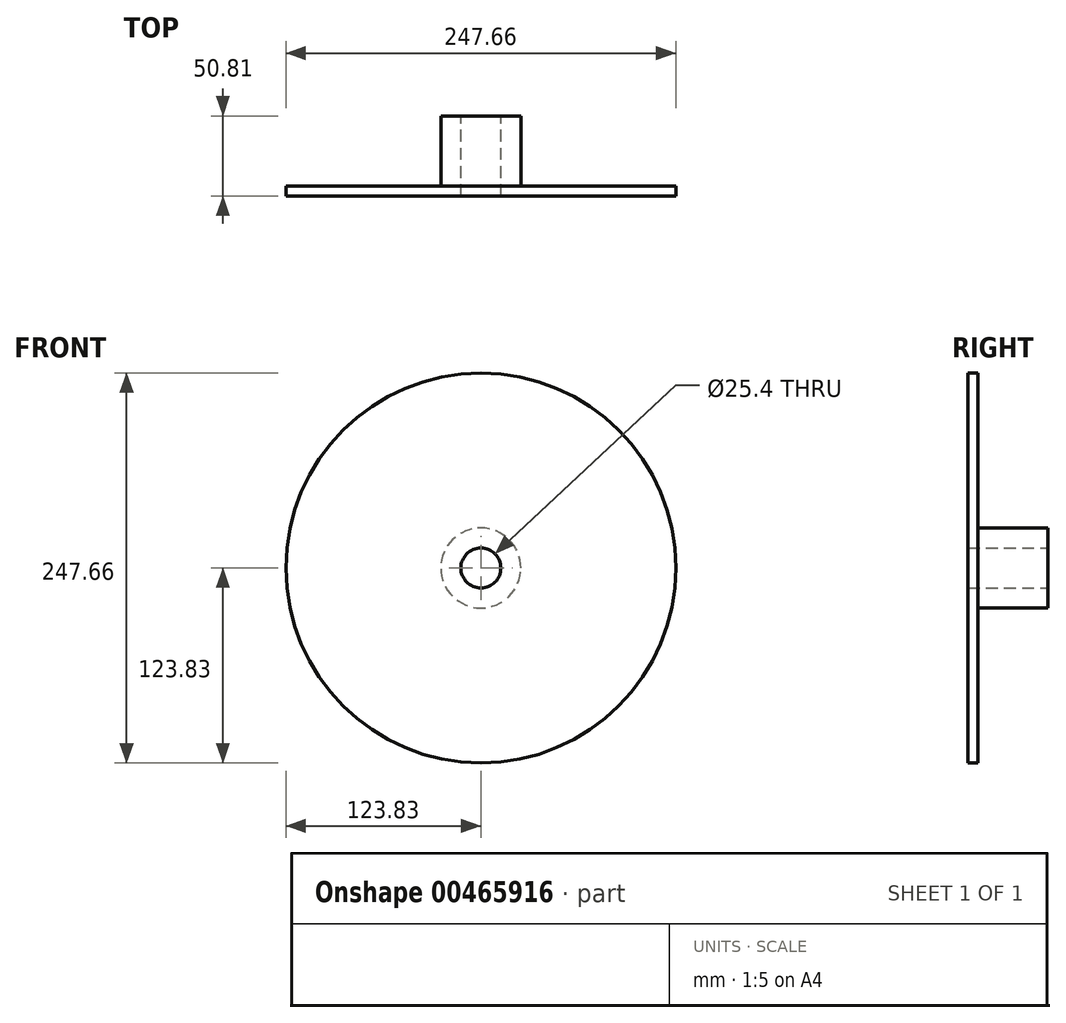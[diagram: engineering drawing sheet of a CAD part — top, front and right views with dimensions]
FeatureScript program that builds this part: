
annotation { "Feature Type Name" : "Feature", "Feature Type Description" : "" }
export const myFeature = defineFeature(function(context is Context, id is Id, definition is map)
    precondition{}
    {
        {
            var Q0;
            Q0=qCreatedBy(makeId("Front.planeOp"),FACE);
            var sketch = newSketch(context, id + "F0", { "sketchPlane" : qUnion([Q0])});
            skCircle(sketch, "E0", {"center": v(0, 0) * mm, "radius": 123.83 * mm});
            skSolve(sketch);
        }
        {
            var Q0;
            Q0=makeQuery(id+"F0.imprint","IMPRINT",FACE,{"disambiguationData":[TD([[makeQuery(id+"F0.imprint","IMPRINT",EDGE,{"derivedFrom":sQuery(id+"F0.wireOp",EDGE,"E0")}),1.0]])]});
            extrude(context, id + "F1", {"entities" : qUnion([Q0]), "endBound" : BoundingType.SYMMETRIC, "depth" : 6.35 * mm});
        }
        {
            var Q0;
            Q0=makeQuery(id+"F1.opExtrude","CAP_FACE",FACE,{"disambiguationData":[OSD([sQuery(id+"F0.wireOp",EDGE,"E0")])],"isStart":false});
            var sketch = newSketch(context, id + "F2", { "sketchPlane" : qUnion([Q0])});
            skCircle(sketch, "E1", {"center": v(0, 0) * mm, "radius": 25.4 * mm});
            skSolve(sketch);
        }
        {
            var Q0;
            Q0=makeQuery(id+"F2.imprint","IMPRINT",FACE,{"disambiguationData":[TD([[makeQuery(id+"F2.imprint","IMPRINT",EDGE,{"derivedFrom":sQuery(id+"F2.wireOp",EDGE,"E1")}),1.0]])]});
            extrude(context, id + "F3", {"entities" : qUnion([Q0]), "operationType" : NewBodyOperationType.ADD, "depth" : -50.8 * mm});
        }
        {
            var Q0;
            Q0=makeQuery(id+"F1.opExtrude","CAP_FACE",FACE,{"disambiguationData":[OSD([sQuery(id+"F0.wireOp",EDGE,"E0")])],"isStart":false});
            var sketch = newSketch(context, id + "F4", { "sketchPlane" : qUnion([Q0])});
            skCircle(sketch, "E2", {"center": v(0, 0) * mm, "radius": 12.7 * mm});
            skSolve(sketch);
        }
        {
            var Q0;
            Q0=makeQuery(id+"F4.imprint","IMPRINT",FACE,{"disambiguationData":[TD([[makeQuery(id+"F4.imprint","IMPRINT",EDGE,{"derivedFrom":sQuery(id+"F4.wireOp",EDGE,"E2")}),1.0]])]});
            extrude(context, id + "F5", {"entities" : qUnion([Q0]), "operationType" : NewBodyOperationType.REMOVE, "endBound" : BoundingType.SYMMETRIC, "depth" : 127 * mm});
        }
    });
